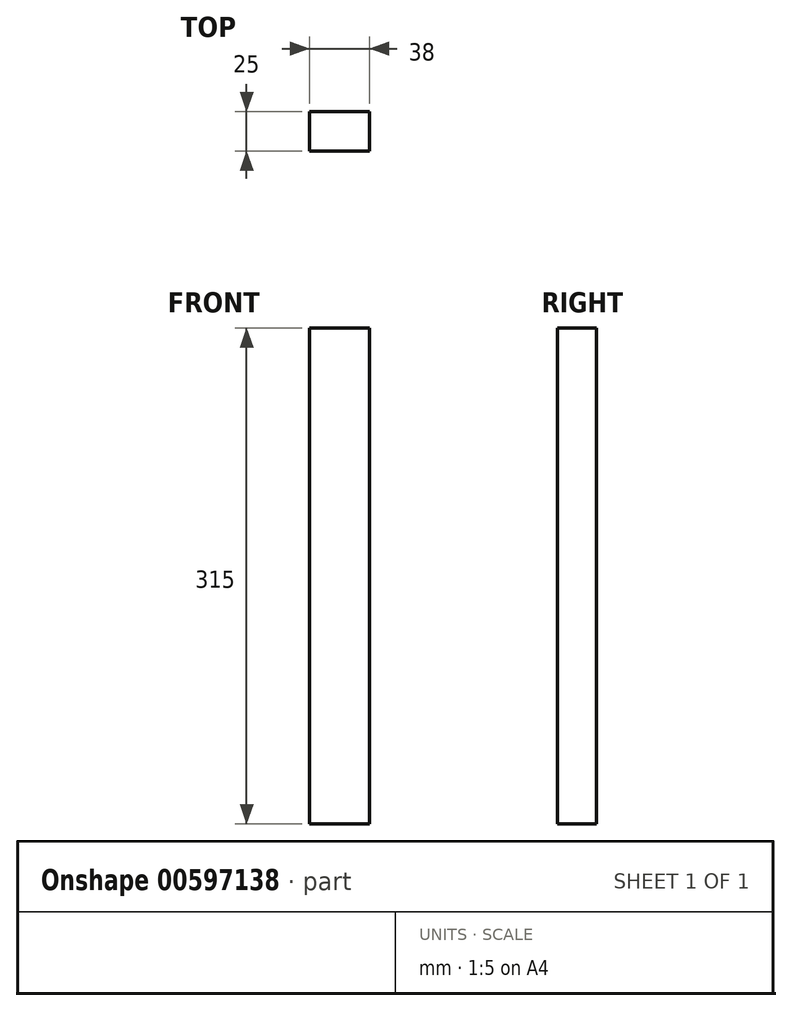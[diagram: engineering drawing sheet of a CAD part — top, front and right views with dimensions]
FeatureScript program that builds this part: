
annotation { "Feature Type Name" : "Feature", "Feature Type Description" : "" }
export const myFeature = defineFeature(function(context is Context, id is Id, definition is map)
    precondition{}
    {
        {
            var Q0;
            Q0=qCreatedBy(makeId("Top.planeOp"),FACE);
            var sketch = newSketch(context, id + "F0", { "sketchPlane" : qUnion([Q0])});
            skLineSegment(sketch, "E0.bottom", {"start": v(19, 12.5) * mm, "end": v(-19, 12.5) * mm});
            skLineSegment(sketch, "E0.top", {"start": v(19, -12.5) * mm, "end": v(-19, -12.5) * mm});
            skLineSegment(sketch, "E0.left", {"start": v(19, 12.5) * mm, "end": v(19, -12.5) * mm});
            skLineSegment(sketch, "E0.right", {"start": v(-19, 12.5) * mm, "end": v(-19, -12.5) * mm});
            skPoint(sketch, "E0.middle", {"position": v(0, 0) * mm});
            skSolve(sketch);
        }
        {
            var Q0;
            Q0 = qSketchRegion(id + "F0", true);
            extrude(context, id + "F1", {"entities" : qUnion([Q0]), "depth" : (340 - 25) * mm, "offsetDistance" : 25 * mm});
        }
    });
